# Revit family: QF_ELECTROLUXPROFESSIONAL_391084_E9FRGD1JFT
name_source: partatom
category: Specialty Equipment
revit_build: Autodesk Revit 2018 (Build: 20190510_1515(x64)
units: mm (PartAtom-declared; Revit-internal decimal feet)

## family parameters
Always vertical = Yes
Cut with Voids When Loaded = No
Part Type = Normal
Room Calculation Point = No
Round Connector Dimension = Use Diameter
Shared = No
Work Plane-Based = No

## types (1)
- QF_ELECTROLUXPROFESSIONAL_391084_E9FRGD1JFT
    Depth = 930 mm  [stored 3.05118 ft]
    Description = 900XP ONE 23 LT WELL GAS TUBE FRYER - LPG/ NATURAL GAS
    Direct Waste Size = 0"
    Gas Connection Height = 0 mm  [stored 0 ft]
    Gas Input = 64771.0 Btu/h
    Gas KW = 19
    Gas Size = 1"
    HP = 0 HP
    Height = 851 mm
    Manufacturer = ELECTROLUX
    Model = 391084
    URL = www.electrolux.com/foodservice
    URL Cutsheet = www.electrolux.com/foodservice
    Watts = 0 W
    Weight in Pounds = 65
    Width = 400 mm  [stored 1.31234 ft]

note: [stored X ft] marks values corroborated as IEEE doubles in the binary element streams (Revit-internal decimal feet)

## geometry (parser evidence)
native form markers: Blend x3, Sweep x2
no freeform markers — native parametric forms only
